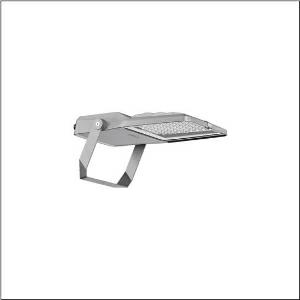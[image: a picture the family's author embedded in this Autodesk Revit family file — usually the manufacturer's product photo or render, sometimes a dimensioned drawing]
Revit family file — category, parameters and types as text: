
# Revit family: floodlight_fl_21_iq_mini___pl43_5xa7772c2a1a_250e
name_source: partatom
category: Lighting Fixtures
units: mm (PartAtom-declared; Revit-internal decimal feet)

## family parameters
Cut with Voids When Loaded = No
Host = Face
Light Source = No
Part Type = Normal
Room Calculation Point = No
Round Connector Dimension = Use Diameter
Shared = No

## types (1)
- --- (1 x LED, 12520 lm, 87.2 W, 3000K)
    Apparent Load = 87 VA
    CIE Flux Codes = 27 78 99 100 100
    Color Rendering = 70
    Color Temperature = 3000K
    Default Elevation = 1800 mm
    Description = Floodlight FL 21 iQ mini, floodlight, primary light control with lens, of PMMA, primary optical cover: protective disc, of toughened safety glass, transparent, light distribution: PL43, light emission: direct distribution, installation type: surface-mounted, lamps: LED, High Power LED, rated values: 12.520lm | 87,2W | 143,6lm/W (begin service life); end service life: 12.520lm | 92,1W; at 50% lumin. flux: 6.260lm | 40,1W | 156,1lm/W, colour temperature: 3000K, colour rendering: CRI > 70, light colour: 730, light setting 1 begin service life: 100% | 12.520lm | 87,2W | 143,6lm/W | 3.000K, light setting 1 end service life: 92,1W, further light settings possible, control: Street-Remote, Auto-Match, Temp-Guard, Night-Set, Smart-Wire, Desk-Remote (wireless, voltage-free reading and setting of iQ features in the workshop via application-optimized NFC function/RFID function), optimised constant luminous flux control (CLO 2.0), pre-setting: linear dimming characteristic, with terminal, 6-pole, mains connection: 220..240V, AC, 50/60Hz, luminaire housing, of diecast aluminium, powder-coated, SITECO metallic grey (DB 702S), corrosivity category C5 mid according to DIN EN ISO 12944suitable for swimming poolschlorine-resistant, sealing non-destructively replaceable, mounting bracket, of steel, galvanised, powder-coated, SITECO metallic grey (DB 702S), protection rating (complete): IP66, insulation class (complete): insulation class II (safety insulation), certification: CE, ENEC, VDE, protection symbol: D, impact resistance: IK08, permissible operating ambient temperature: -40..+40°C, permissible operating ambient temperature for outdoor applications: -40..+50°C, standard: DIN EN 12944, LABS conformity tested according to VDMA 24364:2018-05, packaging unit: 1 piece

Light Distribution: PL43
    Height = 70 mm
    Lamp = 1 x LED
    Lamp Light Flux = 12520 lm
    Lamp Power = 87.2 W
    Lamp count = 1
    Length = 485 mm
    Luminous efficacy = 144 lm/W
    Manufacturer = Siteco
    ModVariant = No
    Model = 5XA7772C2A1A
    Number of Poles = 1
    OnlyDefault = Yes
    Power Factor = 1
    Product Name = Floodlight FL 21 iQ mini | PL43
    Product group = floodlight | pylon annexe
    ProductGroupID = 6201
    Protection Class = Protection class II
    Protection Degree = IP 66
    RLX_Detail_Level = 1
    RLX_Emergency_Light_Flux = 0 lm
    RLX_Emergency_Type = 0
    RLX_Emergency_Type_DB = No
    RlxData = <blob elided: 96509 chars, md5=7df395a3>
    Socket = socket
    Standby Power = 0 W
    System Light Flux = 12520 lm
    System Power = 87 W
    Type Comments = factory setting: luminous flux: 100 % | dim-lin: 254 | 456 mA
    Type Image = l_1006845.jpg
    URL = http://relux.com
    VarID = @adj_162035
    Voltage = 0 V
    Weight = 0.00 kg
    Width = 337 mm

## geometry (parser evidence)
native form markers: Blend x4, Sweep x10
no freeform markers — native parametric forms only
